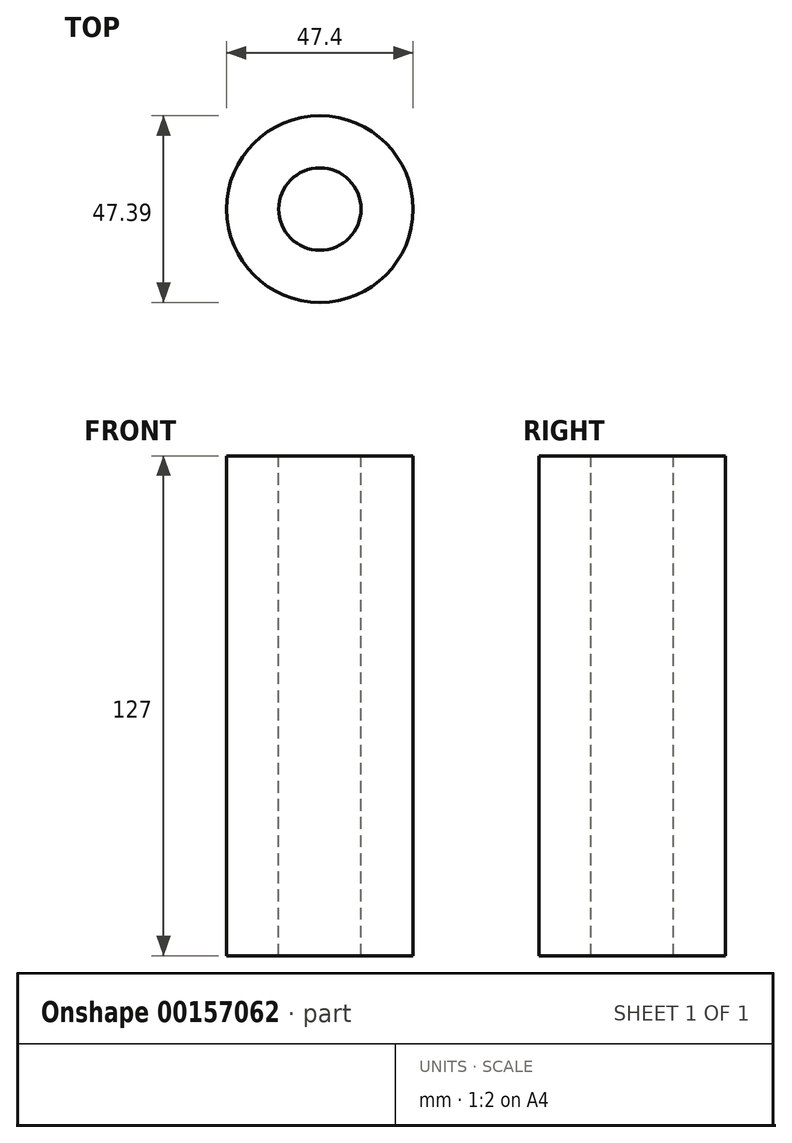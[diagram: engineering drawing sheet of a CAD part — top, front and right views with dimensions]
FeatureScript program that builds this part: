
annotation { "Feature Type Name" : "Feature", "Feature Type Description" : "" }
export const myFeature = defineFeature(function(context is Context, id is Id, definition is map)
    precondition{}
    {
        {
            var Q0;
            Q0=qCreatedBy(makeId("Top.planeOp"),FACE);
            var sketch = newSketch(context, id + "F0", { "sketchPlane" : qUnion([Q0])});
            skLineSegment(sketch, "E0", {"start": v(-75.36, -96.22) * mm, "end": v(106.7, -96.22) * mm});
            skLineSegment(sketch, "E1", {"start": v(-75.36, -96.22) * mm, "end": v(-75.36, 73.68) * mm});
            skLineSegment(sketch, "E2", {"start": v(-75.36, 73.68) * mm, "end": v(107.87, 73.68) * mm});
            skLineSegment(sketch, "E3", {"start": v(107.87, 73.68) * mm, "end": v(106.7, -96.22) * mm});
            skLineSegment(sketch, "E4", {"start": v(107.87, 73.68) * mm, "end": v(-75.36, 73.68) * mm});
            skLineSegment(sketch, "E5", {"start": v(-75.36, 73.68) * mm, "end": v(-75.36, -96.22) * mm});
            skLineSegment(sketch, "E6", {"start": v(106.7, -96.22) * mm, "end": v(107.87, 73.68) * mm});
            skSolve(sketch);
        }
        {
            var Q0;
            Q0=makeQuery(id+"F0.imprint","IMPRINT",FACE,{"disambiguationData":[TD([[makeQuery(id+"F0.imprint","IMPRINT",EDGE,{"derivedFrom":sQuery(id+"F0.wireOp",EDGE,"E0")}),1.0]])]});
            var sketch = newSketch(context, id + "F1", { "sketchPlane" : qUnion([Q0])});
            skLineSegment(sketch, "E7", {"start": v(-75.7, -94.89) * mm, "end": v(-148.86, 27.91) * mm});
            skLineSegment(sketch, "E8", {"start": v(105.86, -94.8) * mm, "end": v(-148.86, 27.91) * mm});
            skLineSegment(sketch, "E9", {"start": v(-148.86, 27.91) * mm, "end": v(34.55, 27.91) * mm});
            skLineSegment(sketch, "E10", {"start": v(34.55, 27.91) * mm, "end": v(105.86, -94.8) * mm});
            skLineSegment(sketch, "E11", {"start": v(34.55, 27.91) * mm, "end": v(108.58, 74.76) * mm});
            skLineSegment(sketch, "E12", {"start": v(-148.86, 27.91) * mm, "end": v(-74.15, 72.42) * mm});
            skLineSegment(sketch, "E13", {"start": v(-75.7, -94.89) * mm, "end": v(34.55, 27.91) * mm});
            skSolve(sketch);
        }
        {
            var Q0;
            {var subQ7=sQuery(id+"F1.wireOp",EDGE,"E10");Q0=makeQuery(id+"F1.imprint","IMPRINT",FACE,{"disambiguationData":[TD([[makeQuery(id+"F1.imprint","IMPRINT",EDGE,{"derivedFrom":subQ7}),1.0]])]});}
            var sketch = newSketch(context, id + "F2", { "sketchPlane" : qUnion([Q0])});
            skCircle(sketch, "E14", {"center": v(-19.9, -33.37) * mm, "radius": 23.7 * mm});
            skCircle(sketch, "E15", {"center": v(-19.9, -33.37) * mm, "radius": 10.47 * mm});
            skSolve(sketch);
        }
        {
            var Q0;
            Q0=sQuery(id+"F2.wireOp",EDGE,"E15");
            var Q1;
            Q1=sQuery(id+"F2.wireOp",EDGE,"E14");
            extrude(context, id + "F3", {"bodyType" : ToolBodyType.SURFACE, "surfaceEntities" : qUnion([Q0, Q1]), "depth" : 63.5 * mm, "hasSecondDirection" : true, "secondDirectionOppositeDirection" : true, "secondDirectionDepth" : 63.5 * mm});
        }
    });
